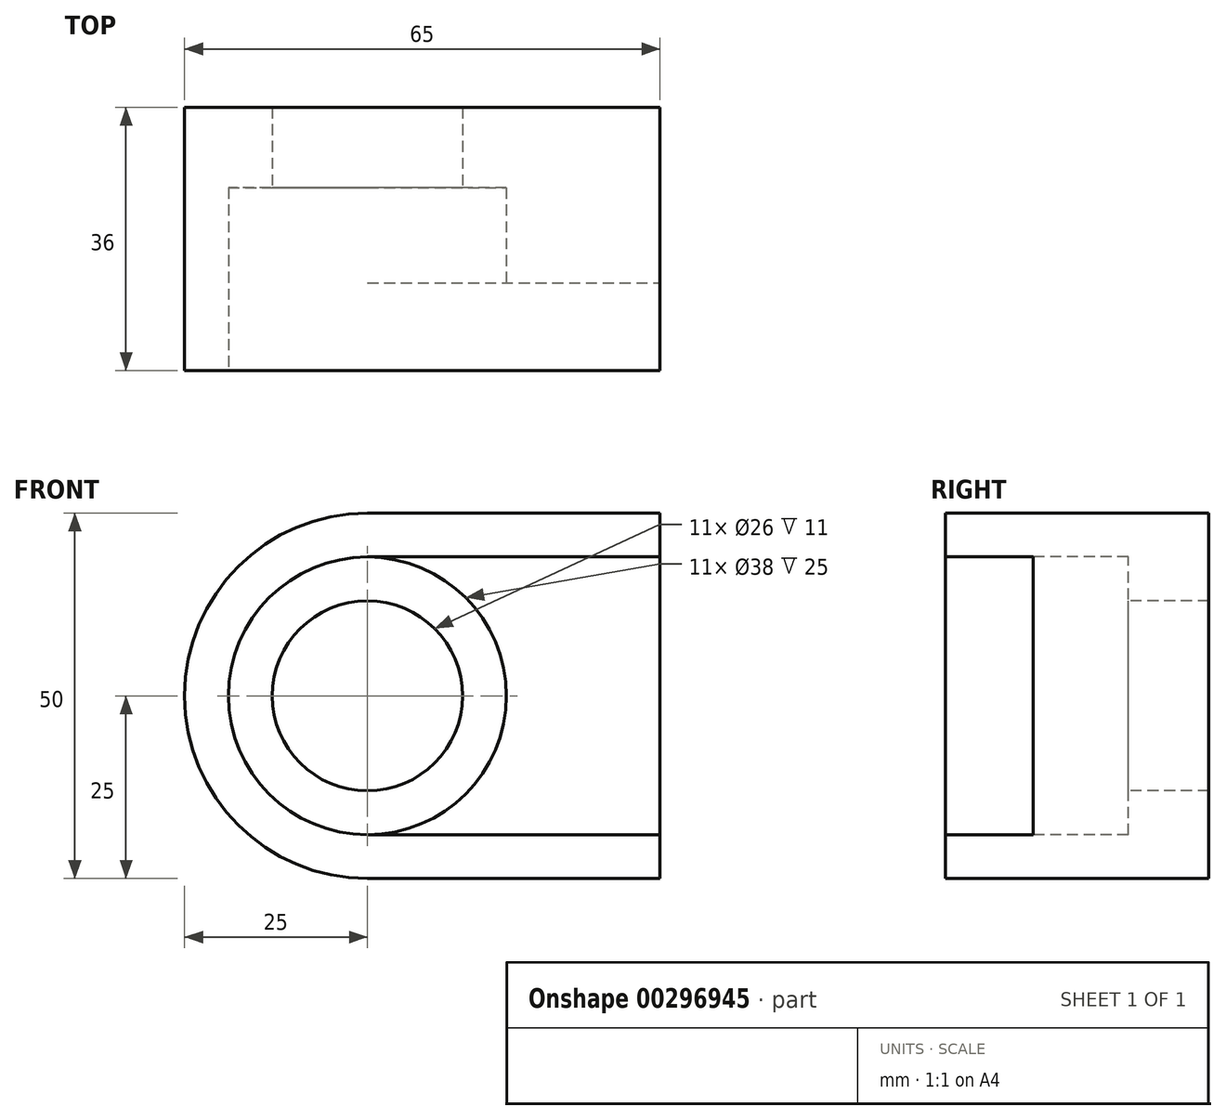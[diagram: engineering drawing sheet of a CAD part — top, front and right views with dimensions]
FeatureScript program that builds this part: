
annotation { "Feature Type Name" : "Feature", "Feature Type Description" : "" }
export const myFeature = defineFeature(function(context is Context, id is Id, definition is map)
    precondition{}
    {
        {
            var Q0;
            Q0=qCreatedBy(makeId("Front.planeOp"),FACE);
            var sketch = newSketch(context, id + "F0", { "sketchPlane" : qUnion([Q0])});
            skCircle(sketch, "E0", {"center": v(0, 0) * mm, "radius": 13 * mm});
            skCircle(sketch, "E1", {"center": v(0, 0) * mm, "radius": 19 * mm});
            skArc(sketch, "E2", {"start": v(0, 25) * mm, "mid": v(-25, 0) * mm, "end": v(0, -25) * mm});
            skLineSegment(sketch, "E3", {"start": v(0, 25) * mm, "end": v(40, 25) * mm});
            skLineSegment(sketch, "E4", {"start": v(40, 25) * mm, "end": v(40, -25) * mm});
            skLineSegment(sketch, "E5", {"start": v(40, -25) * mm, "end": v(0, -25) * mm});
            skLineSegment(sketch, "E6", {"start": v(0, 19) * mm, "end": v(40, 19) * mm});
            skLineSegment(sketch, "E7", {"start": v(0, -19) * mm, "end": v(40, -19) * mm});
            skSolve(sketch);
        }
        {
            var Q0;
            Q0 = qSketchRegion(id + "F0", true);
            var Q1;
            Q1=makeQuery(id+"F0.imprint","IMPRINT",FACE,{"disambiguationData":[TD([[makeQuery(id+"F0.imprint","IMPRINT",EDGE,{"derivedFrom":sQuery(id+"F0.wireOp",EDGE,"E0")}),-1.0]])]});
            extrude(context, id + "F1", {"entities" : qUnion([Q0, Q1]), "oppositeDirection" : true, "depth" : 36 * mm});
        }
        {
            var Q0;
            Q0=makeQuery(id+"F0.imprint","IMPRINT",FACE,{"disambiguationData":[TD([[makeQuery(id+"F0.imprint","IMPRINT",EDGE,{"derivedFrom":sQuery(id+"F0.wireOp",EDGE,"E0")}),-1.0]])]});
            var Q1;
            {var subQ0=sQuery(id+"F0.wireOp",EDGE,"E6");Q1=makeQuery(id+"F0.imprint","IMPRINT",FACE,{"disambiguationData":[TD([[makeQuery(id+"F0.imprint","IMPRINT",EDGE,{"derivedFrom":subQ0}),-1.0]])]});}
            extrude(context, id + "F2", {"entities" : qUnion([Q0, Q1]), "operationType" : NewBodyOperationType.REMOVE, "oppositeDirection" : true, "depth" : 12 * mm});
        }
        {
            var Q0;
            Q0=makeQuery(id+"F0.imprint","IMPRINT",FACE,{"disambiguationData":[TD([[makeQuery(id+"F0.imprint","IMPRINT",EDGE,{"derivedFrom":sQuery(id+"F0.wireOp",EDGE,"E0")}),-1.0]])]});
            extrude(context, id + "F3", {"entities" : qUnion([Q0]), "operationType" : NewBodyOperationType.REMOVE, "oppositeDirection" : true, "depth" : 25 * mm});
        }
    });
